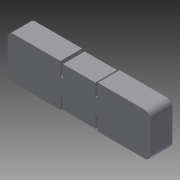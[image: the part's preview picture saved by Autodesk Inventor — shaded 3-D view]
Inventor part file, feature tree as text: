
AUTODESK INVENTOR PART (.ipt)
format: ipt  version: 2015 (Build 190159000, 159)  size: 105,472 bytes
history: native  units: in
note: dims shown in document units (in); Inventor stores cm internally (conversion verified against a paired STEP export)
features: mirror x2, extrude x1, sketch x1
ambient origin geometry x8: Origin, YZ Plane, XZ Plane, XY Plane, X Axis, Y Axis, Z Axis, Center Point
bodies: Solid1 (feature_tree)
feature tree (4):
  extrude  "Extrusion1"  Depth=0.85in
  mirror  "Mirror1"
  mirror  "Mirror2"
  sketch  "Sketch1"  dims[d2=0.1in d10=0.85in d12=0.35in d13=0.0in]
